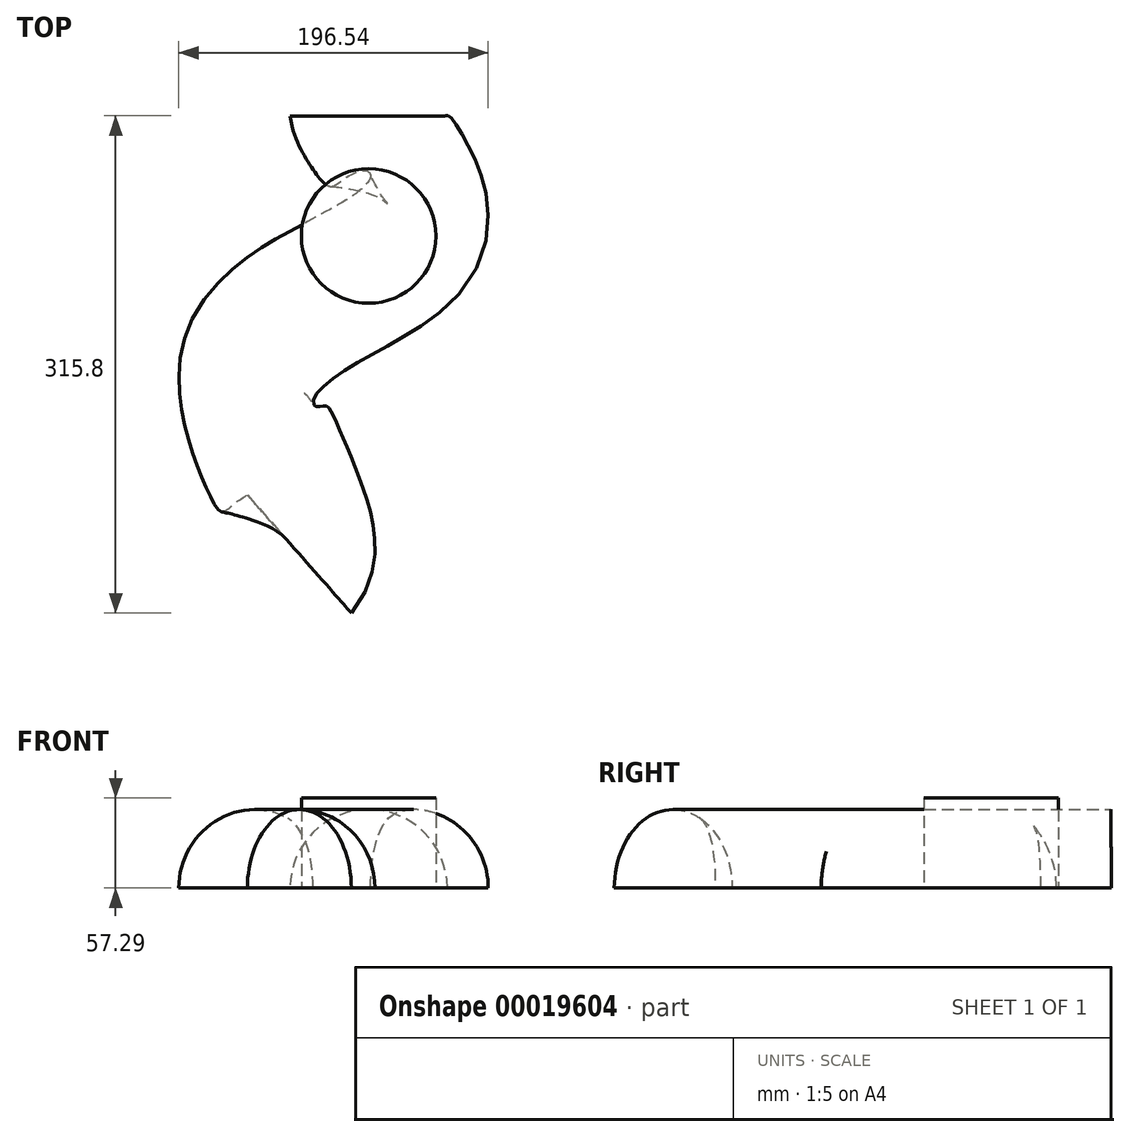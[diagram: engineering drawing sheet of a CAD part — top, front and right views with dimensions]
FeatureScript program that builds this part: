
annotation { "Feature Type Name" : "Feature", "Feature Type Description" : "" }
export const myFeature = defineFeature(function(context is Context, id is Id, definition is map)
    precondition{}
    {
        {
            var Q0;
            Q0=qCreatedBy(makeId("Top.planeOp"),FACE);
            var sketch = newSketch(context, id + "F0", { "sketchPlane" : qUnion([Q0])});
            skCircle(sketch, "E0", {"center": v(0, 0) * mm, "radius": 42.72 * mm});
            skSolve(sketch);
        }
        {
            var Q0;
            Q0=makeQuery(id+"F0.imprint","IMPRINT",FACE,{"disambiguationData":[TD([[makeQuery(id+"F0.imprint","IMPRINT",EDGE,{"derivedFrom":sQuery(id+"F0.wireOp",EDGE,"E0")}),1.0]])]});
            extrude(context, id + "F1", {"entities" : qUnion([Q0]), "depth" : 57.3 * mm});
        }
        {
            var Q0;
            Q0=qCreatedBy(makeId("Front.planeOp"),FACE);
            cPlane(context, id + "F2", {"entities" : qUnion([Q0]), "cplaneType" : CPlaneType.OFFSET, "offset" : 76.2 * mm, "oppositeDirection" : true, "width" : 152.4 * mm, "height" : 152.4 * mm});
        }
        {
            var Q0;
            Q0=qCreatedBy(id+"F2.planeOp",FACE);
            var sketch = newSketch(context, id + "F3", { "sketchPlane" : qUnion([Q0])});
            skArc(sketch, "E1", {"start": v(49.92, 0) * mm, "mid": v(0, 49.92) * mm, "end": v(-49.92, 0) * mm});
            skLineSegment(sketch, "E2", {"start": v(-49.92, 0) * mm, "end": v(49.92, 0) * mm});
            skSolve(sketch);
        }
        {
            var Q0;
            Q0=qCreatedBy(makeId("Top.planeOp"),FACE);
            var sketch = newSketch(context, id + "F4", { "sketchPlane" : qUnion([Q0])});
            skFitSpline(sketch, "E3", {"points": [v(0, 72.43) * mm, v(24.97, 3.02) * mm, v(-71.7, -80.2) * mm, v(-46.86, -204.48) * mm], "startDerivative": vector(80.27, -205.73) * mm, "endDerivative": vector(-97.34, -188.7) * mm});
            skSolve(sketch);
        }
        {
            var Q0;
            Q0=makeQuery(id+"F3.imprint","IMPRINT",FACE,{"disambiguationData":[TD([[makeQuery(id+"F3.imprint","IMPRINT",EDGE,{"derivedFrom":sQuery(id+"F3.wireOp",EDGE,"E1")}),1.0]])]});
            var Q1;
            Q1=sQuery(id+"F4.wireOp",EDGE,"E3");
            sweep(context, id + "F5", {"profiles" : qUnion([Q0]), "path" : qUnion([Q1])});
        }
    });
